# Revit family: Gira_530100
name_source: partatom
category: Elektroinstallationen
revit_build: Autodesk Revit 2017 (Build: 20160225_1515(x64)
units: mm (PartAtom-declared; Revit-internal decimal feet)

## family parameters
Basisbauteil = Fläche
Beim Laden mit Abzugskörper schneiden = Nein
Bemaßung runder Anschluss = Durchmesser verwenden
Beschriftungsausrichtung beibehalten = Nein
Gemeinsam genutzt = Nein
Raumberechnungspunkt = Nein
Teiletyp = Normal

## types (1)
- Server REG Gira eNet
    Art des Zubehörs = sonstige
    BIM = https://media.live.bim.site 00_REG 6.rfa
    BIMSITE_PRODUCT_ID = 34688062b31a76825875535aa20c87b21f15bcc9
    Beschreibung = eNet Server  REG Merkmale:  Visualisierungsserver eNet SMART HOME.  Visualisierung für iOS und Android Smartphones.  Visualisierung für iOS und Android Tablets.  Visualisierung für Gira G1 mit Türkommunikation und Wetterservice.  Visualisierung des Gira Interfaces über Gira Control 9 Client 2.  Visualisierungsfunktionen (Schalten, Dimmen, DALI, Tasten, Jalousie-, Rollläden-, Markiesensteuerung, tado-Heizungsregelung, Szenen, Statusanzeige, Favoriten, Benachrichtigungen).  Kompatibel zur smarten Heizungssteuerung von tado ab eNet Server Software Version 2.1.  Einfaches anlegen und Konfiguration von bis zu 34 Szenen mit bis zu 100 Aktionen über die Visualisierung.  Einfaches anlegen und Konfiguration von bis zu 100 Zeitschaltuhren mit bis zu 100 Aktionen über die Visualisierung.  Einfaches anlegen und Konfiguration von bis zu 32 Wenn-Dann-regeln mit bis zu 32 Bedingungen, Aktionen, Später-Aktionen über die Visualisierung.  Gleichzeitiger Zugriff von bis zu 8 Visualisierungsgeräten (Smartphone, Tablet, G1, Gira Control 9 Client 2 oder Windows(r) PC.  Bis zu 10 verschiedene Benutzerkonten anlegen.  Einfaches Benutzermanagement über eNet SMART HOME Visualisierung.  Visualisierung von Energiesensoren.     Import   Export von Projektdateien.  Einfacher Projektabgleich über eNet SMART HOME connect.  Update und Konfiguration von eNet SMART HOME Geräten.  Integrierte Telegrammaufzeichnung zur Diagnose.  Automatisch generierte Projektdokumentation.     Funksender und Funkempfänger für max. 32 eNet Funk Reiheneinbaugeräte (kein eNet Funk Empfangsmodul REG erforderlich).  Interne eNet Funk- und WLAN-Antenne.  Externe eNet Funk- und WLAN-Antennen anschließbar.    Hohe Sicherheit:  Vollverschlüsselte Funkübertragung (AES-CCM 128 bit) verhindert das Mitlesen durch Dritte.  Vollverschlüsselter Fernzugriff über My-eNet-Portal (my.enet-smarthome.com) für IPv4 und IPv6 verhindert das Mitlesen durch Dritte.  Vollverschlüsselte Fernwartung über My-eNet-Portal (my.enet-smarthome.com) verhindert das Mitlesen durch Dritte  Hinweise :  Die Installation des eNet Servers ist möglichst an einem zentralen Ort (z. B. Erdgeschoss) vorzunehmen, um eine gute Empfangsqualität zu gewährleisten.  Beim Einbau in Verteilerschrank bzw. Unterverteilung mit Metallgehäuse ist eine Zusatzantenne erforderlich. Die Zusatzantenne ist außerhalb des Metallgehäuses zu platzieren.  Die Inbetriebnahme des Servers erfolgt mit dem Web-Interface eNet SMART HOME connect. Für die Inbetriebnahme über das Web-Interface muss der Inbetriebnahme-Computer über einen aktuellen Browser (z. B. Mozilla Firefox, Microsoft Internet Explorer, Edge, Safari, Chrome) verfügen.  Zur Spannungsversorgung im Verteilerschrank wird die Spannungsversorgung benötigt.  Nicht kompatible zum Gira Funk-Bussystem.  Kompatibilität zur intelligenten Heizungssteuerung von tado ist ab eNet Server Version 2.1 gewährleistet.
    Datenblatt = https://media.live.bim.site
    Datenblatt 1 = https://media.live.bim.site
    GTIN = 4010337591306
    HAN = 530100
    HeinzeBIM = https://www.heinze.de
    Hersteller = Gira
    Ist System = Nein
    Ist Zubehör = Nein
    Kosten = 0 $
    Produktseite = https://media.live.bim.site
    Typname = Server REG Gira eNet
    URL = https://www.gira.de
    Vorgabe-Ansicht = 1219 mm

## geometry (parser evidence)
native form markers: Sweep x1
no freeform markers — native parametric forms only
